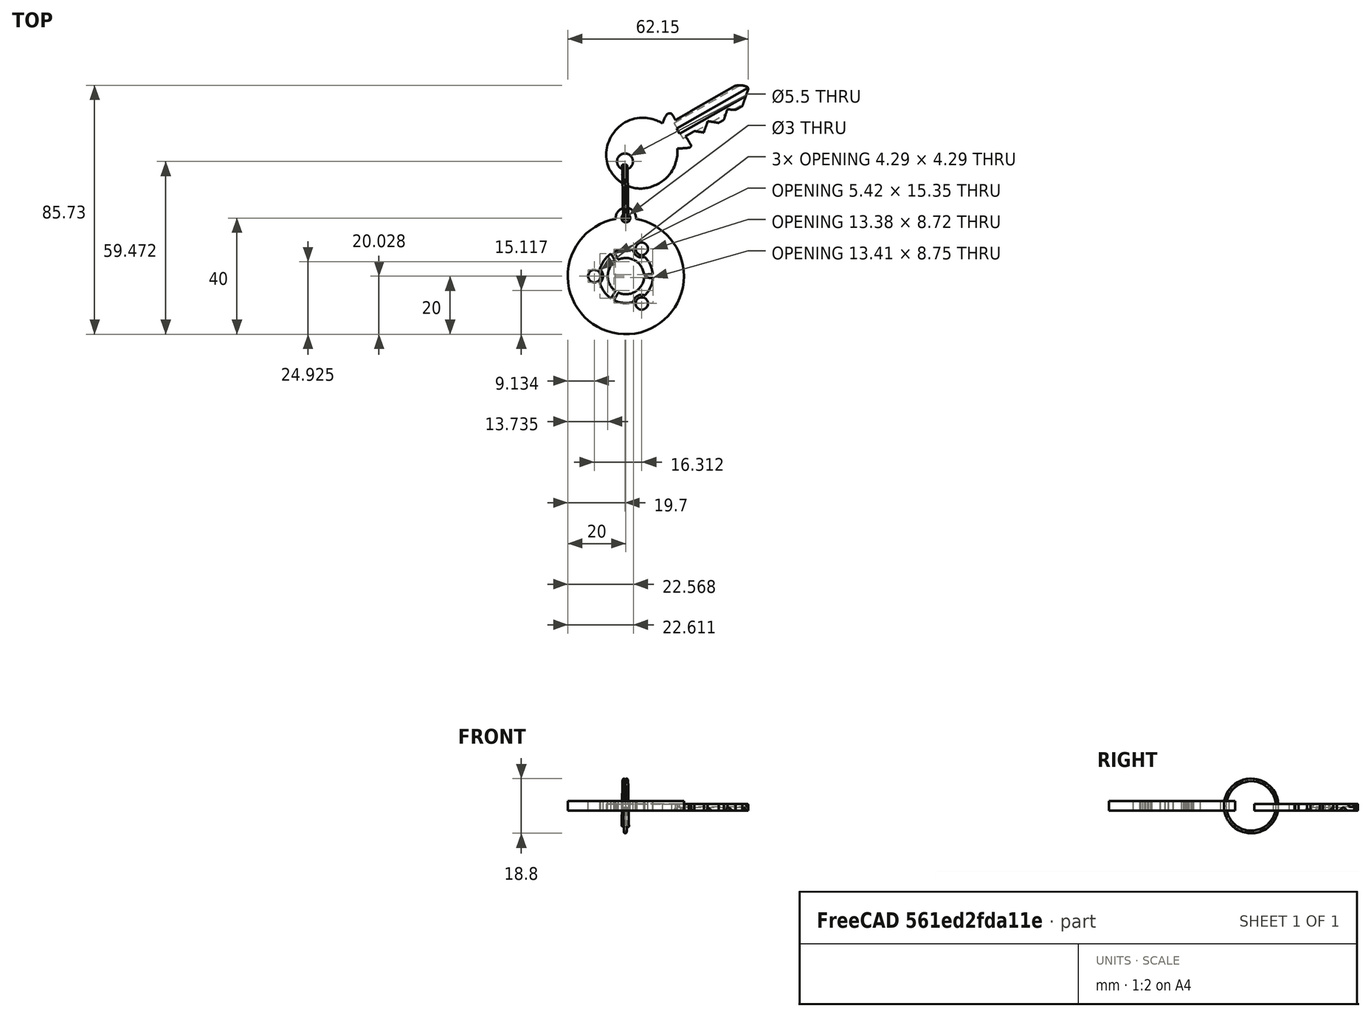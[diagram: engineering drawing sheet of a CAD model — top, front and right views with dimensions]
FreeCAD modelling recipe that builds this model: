
FCSTD DOCUMENT  (FreeCAD 0.14R3703 (Git))
Label: Ubuntu_chain
License: CC-BY 3.0
LicenseURL: http://creativecommons.org/licenses/by/3.0/
objects: Part::Feature×8, Part::Cut×7, Part::Extrusion×6, Part::Cylinder×3, Part::MultiFuse×1
note: 25 computed .brp shape members not serialized (recipe doc carries the construction recipe); baked Part::Feature solids carry a one-line shape summary decoded from their .brp

FEATURE [Part::Feature] Circle
  Placement = pos=(-38.5,0,0) rot=(0,0,1;0rad)
  shape: bbox 4.605 x 4.605 x 2e-07 mm, 1 faces, 0 solids (baked)
FEATURE [Part::Feature] Circle001
  Placement = pos=(19.3,-33.4,0) rot=(0,0,1;0rad)
  shape: bbox 4.605 x 4.605 x 2e-07 mm, 1 faces, 0 solids (baked)
FEATURE [Part::Feature] Path001
  shape: bbox 5.438 x 15.37 x 2e-07 mm, 1 faces, 0 solids (baked)
FEATURE [Part::Feature] Path002
  shape: bbox 13.39 x 8.752 x 2e-07 mm, 1 faces, 0 solids (baked)
FEATURE [Part::Feature] Path003
  shape: bbox 13.42 x 8.779 x 2e-07 mm, 1 faces, 0 solids (baked)
FEATURE [Part::Feature] Circle002
  Placement = pos=(19.3,33.4,0) rot=(0,0,1;0rad)
  shape: bbox 4.605 x 4.605 x 2e-07 mm, 1 faces, 0 solids (baked)
FEATURE [Part::Extrusion] Extrude001  label="Taladro 1"
  Base = -> Circle
  Dir = (0,0,3.3)
  Solid = false
FEATURE [Part::Extrusion] Extrude002  label="Taladro 2"
  Base = -> Circle001
  Dir = (0,0,3.3)
  Solid = false
FEATURE [Part::Extrusion] Extrude003  label="Ranura 1"
  Base = -> Path001
  Dir = (0,0,3.3)
  Solid = false
FEATURE [Part::Extrusion] Extrude004  label="Ranura 2"
  Base = -> Path002
  Dir = (0,0,3.3)
  Solid = false
FEATURE [Part::Extrusion] Extrude005  label="Ranura 3"
  Base = -> Path003
  Dir = (0,0,3.3)
  Solid = false
FEATURE [Part::Extrusion] Extrude006  label="Taladro 3"
  Base = -> Circle002
  Dir = (0,0,3.3)
  Solid = false
FEATURE [Part::Cylinder] Cylinder  label="Cilindro"
  Angle = 360
  Height = 3.3
  Radius = 20
FEATURE [Part::Cylinder] Cylinder001  label="Cilindro001"
  Angle = 360
  Height = 3.3
  Placement = pos=(0,20,0) rot=(0,0,1;0rad)
  Radius = 3.5
FEATURE [Part::MultiFuse] Fusion  label="Base 1"
  Shapes = -> [Cylinder,Cylinder001]
FEATURE [Part::Cylinder] Cylinder002  label="Cilindro002"
  Angle = 360
  Height = 3.3
  Placement = pos=(0,20,0) rot=(0,0,1;0rad)
  Radius = 1.5
FEATURE [Part::Cut] Cut  label="Base 2"
  Base = -> Fusion
  Tool = -> Cylinder002
FEATURE [Part::Cut] Cut001
  Base = -> Cut
  Tool = -> Extrude001
FEATURE [Part::Cut] Cut002
  Base = -> Cut001
  Tool = -> Extrude002
FEATURE [Part::Cut] Cut003
  Base = -> Cut002
  Tool = -> Extrude006
FEATURE [Part::Cut] Cut004
  Base = -> Cut003
  Tool = -> Extrude003
FEATURE [Part::Cut] Cut005
  Base = -> Cut004
  Tool = -> Extrude004
FEATURE [Part::Cut] Cut006  label="Moneda"
  Base = -> Cut005
  Tool = -> Extrude005
FEATURE [Part::Feature] Sweep  label="key-ring-model-1"
  Placement = pos=(-1,29,1.6391) rot=(0.333333,0.881917,0.333333;1.69612rad)
  shape: bbox 3.31 x 27.02 x 26.33 mm, 4 faces (baked)
FEATURE [Part::Feature] Cut007  label="key-model-1"
  Placement = pos=(-5.46976,36.5266,0) rot=(0,0,1;0.517888rad)
  shape: bbox 49.82 x 36.6 x 2.3 mm, 44 faces (baked)
